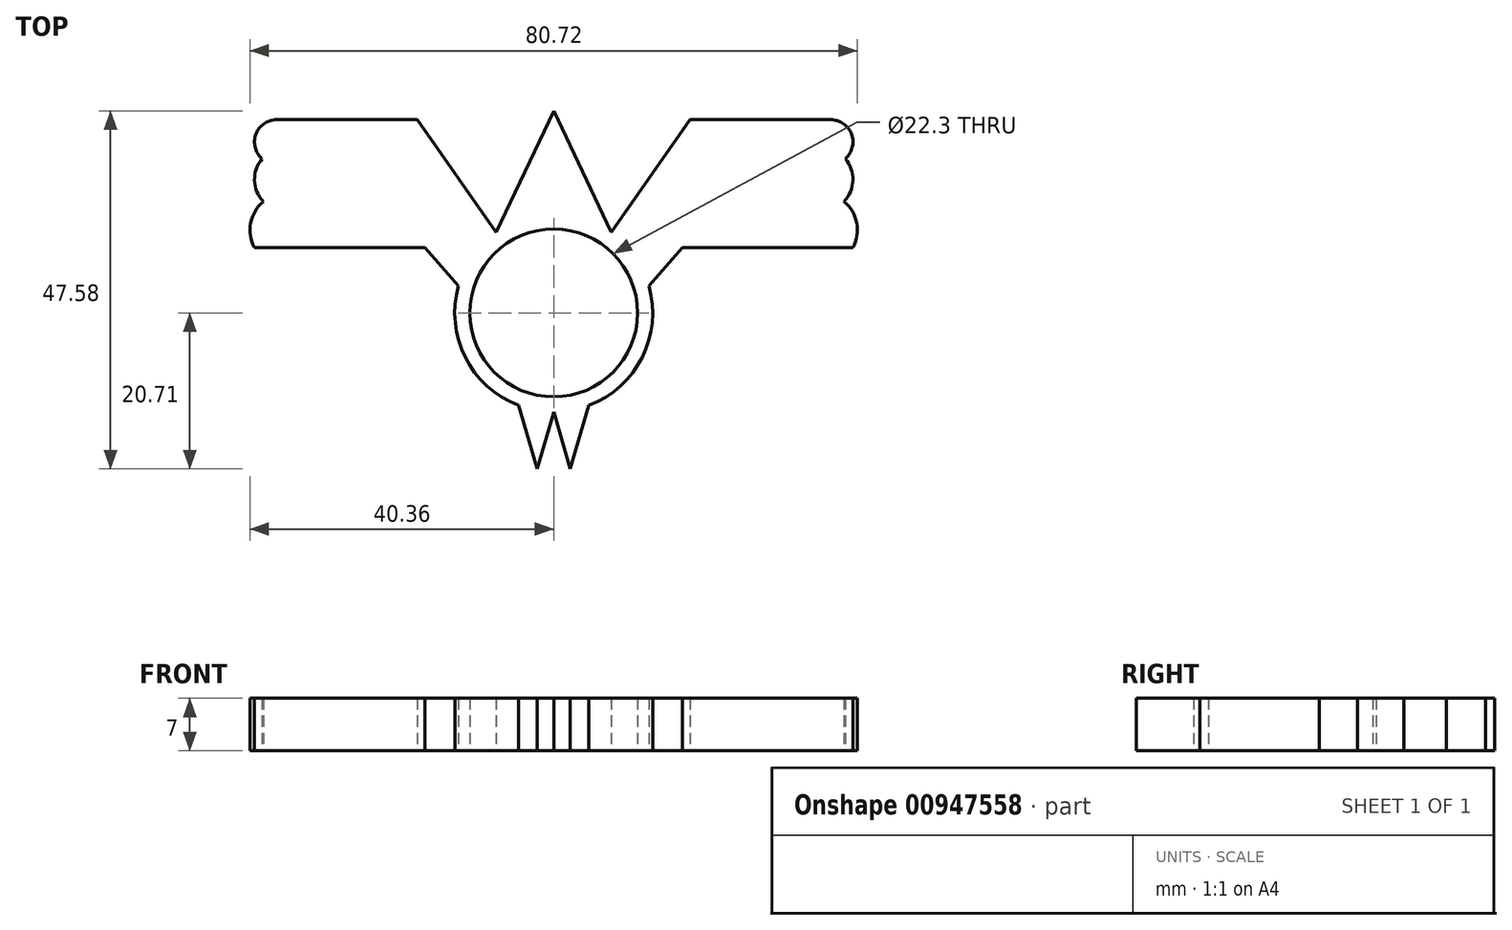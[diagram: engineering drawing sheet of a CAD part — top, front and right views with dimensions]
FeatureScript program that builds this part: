
annotation { "Feature Type Name" : "Feature", "Feature Type Description" : "" }
export const myFeature = defineFeature(function(context is Context, id is Id, definition is map)
    precondition{}
    {
        {
            var Q0;
            Q0=qCreatedBy(makeId("Top.planeOp"),FACE);
            var sketch = newSketch(context, id + "F0", { "sketchPlane" : qUnion([Q0])});
            skCircle(sketch, "E0", {"center": v(0, 0) * mm, "radius": 11.15 * mm});
            skCircle(sketch, "E1.0", {"center": v(0, 0) * mm, "radius": 13.15 * mm});
            skLineSegment(sketch, "E2", {"start": v(0, 26.87) * mm, "end": v(-7.64, 10.7) * mm});
            skLineSegment(sketch, "E3", {"start": v(-7.64, 10.7) * mm, "end": v(-18.1, 25.68) * mm});
            skLineSegment(sketch, "E4", {"start": v(-18.1, 25.68) * mm, "end": v(-36.8, 25.68) * mm});
            skArc(sketch, "E5", {"start": v(-36.8, 25.68) * mm, "mid": v(-39.77, 22.72) * mm, "end": v(-36.8, 19.77) * mm});
            skLineSegment(sketch, "E6", {"start": v(-36.8, 19.77) * mm, "end": v(-18.1, 19.77) * mm});
            skLineSegment(sketch, "E7", {"start": v(-18.1, 19.77) * mm, "end": v(-9.94, 8.6) * mm});
            skLineSegment(sketch, "E8", {"start": v(0, 20.48) * mm, "end": v(-3.82, 12.58) * mm});
            skPoint(sketch, "E8.endSnap0", {"position": v(-3.82, 18.78) * mm});
            skArc(sketch, "E9", {"start": v(-38.75, 20.49) * mm, "mid": v(-39.76, 17.62) * mm, "end": v(-38.58, 14.81) * mm});
            skLineSegment(sketch, "E10", {"start": v(-38.58, 14.81) * mm, "end": v(-14.48, 14.81) * mm});
            skArc(sketch, "E11", {"start": v(-38.58, 14.81) * mm, "mid": v(-40.27, 11.94) * mm, "end": v(-39.77, 8.65) * mm});
            skPoint(sketch, "E11.endSnap0", {"position": v(-39.77, 22.72) * mm});
            skLineSegment(sketch, "E12", {"start": v(-39.77, 8.65) * mm, "end": v(-17.1, 8.65) * mm});
            skLineSegment(sketch, "E13", {"start": v(-17.1, 8.65) * mm, "end": v(-12.65, 3.58) * mm});
            skLineSegment(sketch, "E14", {"start": v(-4.68, -12.29) * mm, "end": v(-2.2, -20.7) * mm});
            skLineSegment(sketch, "E15", {"start": v(-2.2, -20.7) * mm, "end": v(0, -13.15) * mm});
            skLineSegment(sketch, "E16.MirrorCS", {"start": v(0, 26.87) * mm, "end": v(7.64, 10.7) * mm});
            skLineSegment(sketch, "E17.MirrorCS", {"start": v(0, 20.48) * mm, "end": v(3.82, 12.58) * mm});
            skLineSegment(sketch, "E18.MirrorCS", {"start": v(7.64, 10.7) * mm, "end": v(18.1, 25.68) * mm});
            skLineSegment(sketch, "E19.MirrorCS", {"start": v(18.1, 25.68) * mm, "end": v(36.8, 25.68) * mm});
            skLineSegment(sketch, "E20.MirrorCS", {"start": v(36.8, 19.77) * mm, "end": v(18.1, 19.77) * mm});
            skArc(sketch, "E21.MirrorCS", {"start": v(36.8, 25.68) * mm, "mid": v(39.77, 22.72) * mm, "end": v(36.8, 19.77) * mm});
            skArc(sketch, "E22.MirrorCS", {"start": v(38.75, 20.49) * mm, "mid": v(39.76, 17.62) * mm, "end": v(38.58, 14.81) * mm});
            skLineSegment(sketch, "E23.MirrorCS", {"start": v(38.58, 14.81) * mm, "end": v(14.48, 14.81) * mm});
            skLineSegment(sketch, "E24.MirrorCS", {"start": v(18.1, 19.77) * mm, "end": v(9.94, 8.6) * mm});
            skLineSegment(sketch, "E25.MirrorCS", {"start": v(39.77, 8.65) * mm, "end": v(17.1, 8.65) * mm});
            skLineSegment(sketch, "E26.MirrorCS", {"start": v(17.1, 8.65) * mm, "end": v(12.65, 3.58) * mm});
            skArc(sketch, "E27.MirrorCS", {"start": v(38.58, 14.81) * mm, "mid": v(40.27, 11.94) * mm, "end": v(39.77, 8.65) * mm});
            skLineSegment(sketch, "E28.MirrorCS", {"start": v(4.68, -12.29) * mm, "end": v(2.2, -20.7) * mm});
            skLineSegment(sketch, "E29.MirrorCS", {"start": v(2.2, -20.7) * mm, "end": v(0, -13.15) * mm});
            skSolve(sketch);
        }
        {
            var Q0;
            Q0 = qSketchRegion(id + "F0", true);
            var Q1;
            {var subQ0=sQuery(id+"F0.wireOp",EDGE,"E8");Q1=makeQuery(id+"F0.imprint","IMPRINT",FACE,{"disambiguationData":[TD([[makeQuery(id+"F0.imprint","IMPRINT",EDGE,{"derivedFrom":subQ0}),1.0]])]});}
            extrude(context, id + "F1", {"entities" : qUnion([Q0, Q1]), "depth" : 7 * mm, "offsetDistance" : 25 * mm});
        }
    });
